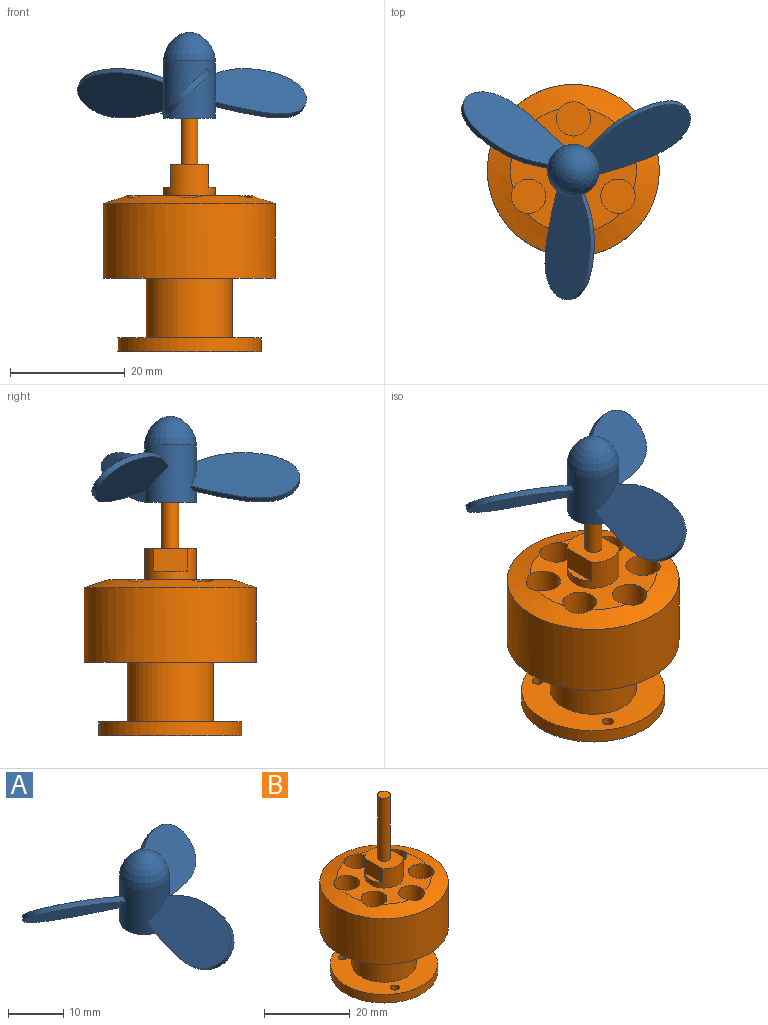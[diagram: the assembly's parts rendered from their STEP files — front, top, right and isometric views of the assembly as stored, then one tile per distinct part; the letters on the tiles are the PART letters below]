
ASSEMBLY  parts=2 mates=1
PART A: 14 faces, bbox 40.7x36.9x15.3 mm
  f0: cylinder r=2mm len=10mm, axis (0,0,-1), area 125.7mm2, adj f2,f4
  f1: cylinder r=4.5mm len=10mm, axis (0,0,-1), area 263.9mm2, adj f2,f3,f5,f6,f7,f8,f9,f10
  f2: plane 9x9mm, normal (0,0,-1), area 51.1mm2, adj f0,f1
  f3: revolved ~9x9mm, area 133.3mm2, adj f1
  f4: plane 4x4mm, normal (0,0,-1), area 12.6mm2, adj f0
  f5: extruded ~19.08x8.62mm, area 43.6mm2, adj f1,f6,f7
  f6: plane 19.32x8.57mm, normal (0.71,0,-0.71), area 166.4mm2, adj f1,f5
  f7: plane 19.5x8.6mm, normal (-0.71,0,0.71), area 166.9mm2, adj f1,f5
  f8: extruded ~17.93x12.84mm, area 43.6mm2, adj f1,f9,f10
  f9: plane 17.99x12.57mm, normal (-0.35,0.61,-0.71), area 166.4mm2, adj f1,f8
  f10: plane 18.02x12.6mm, normal (0.35,-0.61,0.71), area 166.9mm2, adj f1,f8
  f11: extruded ~17.95x13.35mm, area 43.6mm2, adj f1,f12,f13
  f12: plane 17.94x13.08mm, normal (-0.35,-0.61,-0.71), area 166.4mm2, adj f1,f11
  f13: plane 17.99x13.1mm, normal (0.35,0.61,0.71), area 166.9mm2, adj f1,f11
PART B: 33 faces, bbox 30x30x50.7 mm
  f0: plane 6.01x1.15mm, normal (0,0,1), area 4.7mm2, adj f17,f20
  f1: plane 22x21.44mm, normal (0,0,1), area 167.8mm2, adj f4,f5,f7,f9,f11,f13,f15,f17
  f2: cylinder r=15mm len=30mm, axis (0,0,-1), area 1225.2mm2, adj f3,f4
  f3: plane 30x30mm, normal (0,0,-1), area 530.1mm2, adj f2,f24
  f4: cone r=11mm half-angle=70.7deg, axis (0,0,-1), area 324mm2, adj f1,f2,f5,f7,f9,f11,f13,f15
  f5: cylinder r=3mm len=12mm, axis (0,0,1), area 224.9mm2, adj f1,f4,f6
  f6: plane 6x6mm, normal (0,0,1), area 28.3mm2, adj f5
  f7: cylinder r=3mm len=12mm, axis (0,0,1), area 224.9mm2, adj f1,f4,f8
  f8: plane 6x6mm, normal (0,0,1), area 28.3mm2, adj f7
  f9: cylinder r=3mm len=12mm, axis (0,0,1), area 224.9mm2, adj f1,f4,f10
  f10: plane 6x6mm, normal (0,0,1), area 28.3mm2, adj f9
  f11: cylinder r=3mm len=12mm, axis (0,0,1), area 224.9mm2, adj f1,f4,f12
  f12: plane 6x6mm, normal (0,0,1), area 28.3mm2, adj f11
  f13: cylinder r=3mm len=12mm, axis (0,0,1), area 224.9mm2, adj f1,f4,f14
  f14: plane 6x6mm, normal (0,0,1), area 28.3mm2, adj f13
  f15: cylinder r=3mm len=12mm, axis (0,0,1), area 224.9mm2, adj f1,f4,f16
  f16: plane 6x6mm, normal (0,0,1), area 28.3mm2, adj f15
  f17: cylinder r=4.5mm len=9mm, axis (0,0,-1), area 102.9mm2, adj f0,f1,f18,f19,f20,f21
  f18: plane 6.01x1.15mm, normal (0,0,1), area 4.7mm2, adj f17,f19
  f19: plane 6.01x4mm, normal (-1,0,0), area 24mm2, adj f17,f18,f21
  f20: plane 6.01x4mm, normal (1,0,0), area 24mm2, adj f0,f17,f21
  f21: plane 9x6.7mm, normal (0,0,1), area 47.1mm2, adj f17,f19,f20,f22
  f22: cylinder r=1.5mm len=18mm, axis (0,0,-1), area 169.6mm2, adj f21,f23
  f23: plane 3x3mm, normal (0,0,1), area 7.1mm2, adj f22
  f24: cylinder r=7.5mm len=15mm, axis (0,0,1), area 490.1mm2, adj f3,f27
  f25: cylinder r=12.5mm len=25mm, axis (0,0,1), area 188.5mm2, adj f26,f27
  f26: plane 25x25mm, normal (0,0,-1), area 386.4mm2, adj f25,f28,f29,f30,f31
  f27: plane 25x25mm, normal (0,0,1), area 304.7mm2, adj f24,f25,f28,f29,f30
  f28: cylinder r=1mm len=2.4mm, axis (0,0,-1), area 15.1mm2, adj f26,f27
  f29: cylinder r=1mm len=2.4mm, axis (0,0,-1), area 15.1mm2, adj f26,f27
  f30: cylinder r=1mm len=2.4mm, axis (0,0,-1), area 15.1mm2, adj f26,f27
  f31: cylinder r=5.5mm len=11mm, axis (0,0,-1), area 82.9mm2, adj f26,f32
  f32: plane 11x11mm, normal (0,0,-1), area 95mm2, adj f31
PLACE A t=(-22.01,-15.6,11.01)mm
PLACE B t=(-22.01,-15.6,-16.89)mm
MATE revolute A.f0 <-> B.f2  axis (0,0,-1) through (-22.01,-15.6,21.01)mm
